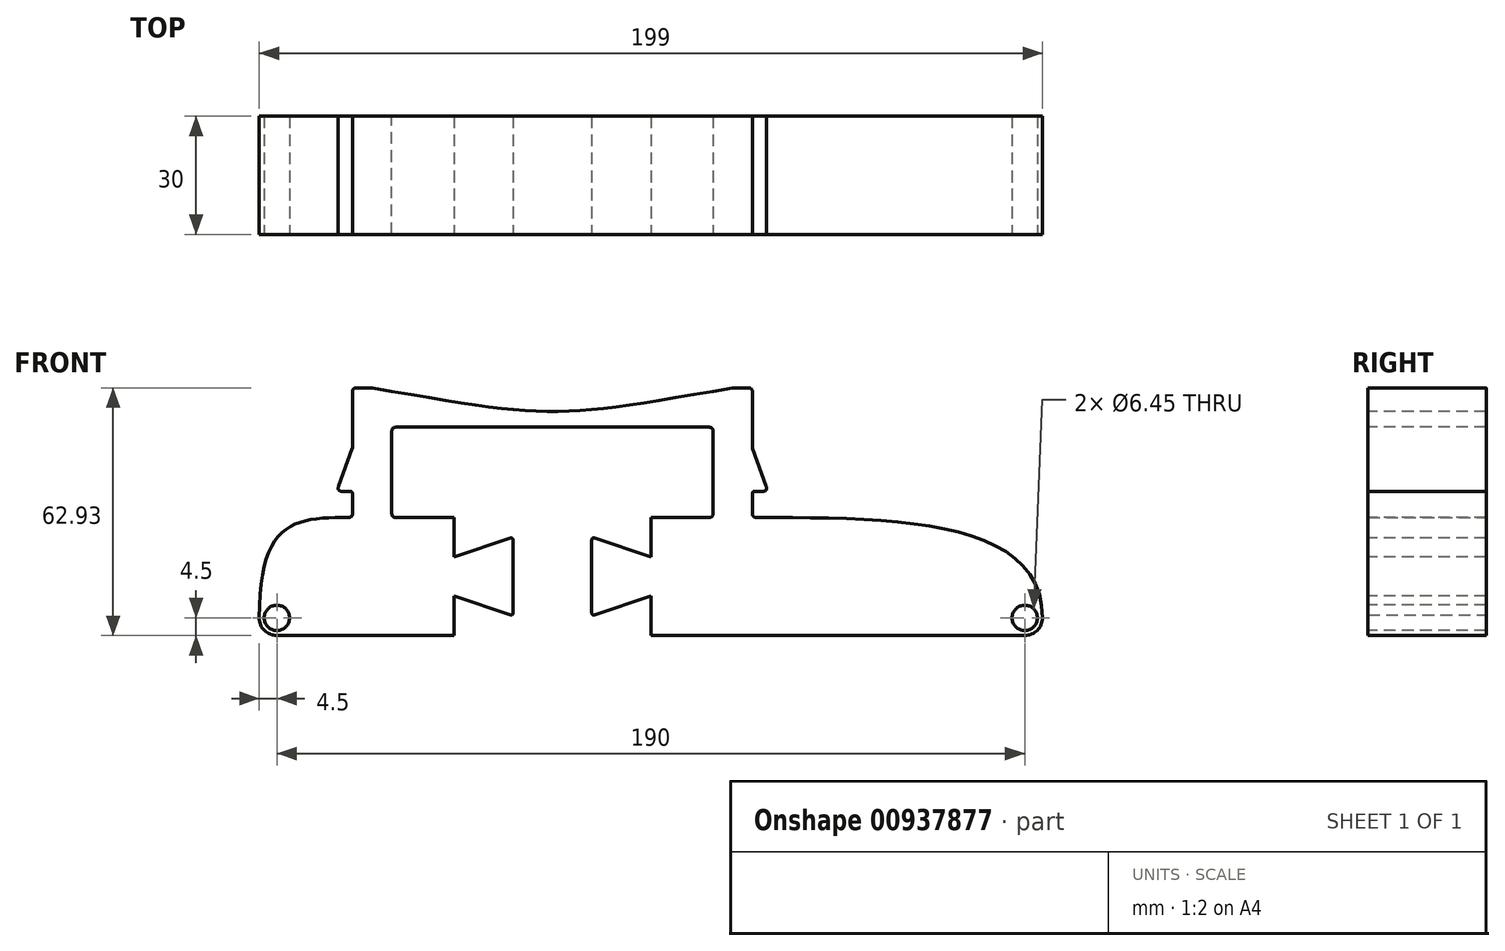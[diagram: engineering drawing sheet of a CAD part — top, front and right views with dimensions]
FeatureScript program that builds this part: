
annotation { "Feature Type Name" : "Feature", "Feature Type Description" : "" }
export const myFeature = defineFeature(function(context is Context, id is Id, definition is map)
    precondition{}
    {
        {
            var Q0;
            Q0=qCreatedBy(makeId("Front.planeOp"),FACE);
            var sketch = newSketch(context, id + "F0", { "sketchPlane" : qUnion([Q0])});
            skLineSegment(sketch, "E0", {"start": v(0, 0) * mm, "end": v(-70, 0) * mm});
            skLineSegment(sketch, "E1", {"start": v(-50.8, 30) * mm, "end": v(-50.8, 36.63) * mm});
            skLineSegment(sketch, "E2", {"start": v(-50.8, 36.63) * mm, "end": v(-52.8, 36.63) * mm});
            skLineSegment(sketch, "E3", {"start": v(-52.8, 36.63) * mm, "end": v(-52.8, 36.63) * mm});
            skLineSegment(sketch, "E4", {"start": v(-52.8, 36.63) * mm, "end": v(-54.8, 36.63) * mm});
            skLineSegment(sketch, "E5", {"start": v(-54.8, 36.63) * mm, "end": v(-54.8, 36.63) * mm});
            skLineSegment(sketch, "E6", {"start": v(-50.8, 47.63) * mm, "end": v(-50.8, 62.93) * mm});
            skPoint(sketch, "E7", {"position": v(-70, 4.5) * mm});
            skCircle(sketch, "E8", {"center": v(-70, 4.5) * mm, "radius": 4.5 * mm});
            skLineSegment(sketch, "E9", {"start": v(-50.8, 30) * mm, "end": v(-73.18, 7.69) * mm});
            skLineSegment(sketch, "E10", {"start": v(50.8, 62.93) * mm, "end": v(50.8, 47.63) * mm});
            skLineSegment(sketch, "E11", {"start": v(54.8, 36.63) * mm, "end": v(52.8, 36.63) * mm});
            skLineSegment(sketch, "E12", {"start": v(52.8, 36.63) * mm, "end": v(52.8, 36.63) * mm});
            skLineSegment(sketch, "E13", {"start": v(52.8, 36.63) * mm, "end": v(50.8, 36.63) * mm});
            skLineSegment(sketch, "E14", {"start": v(50.8, 36.63) * mm, "end": v(50.8, 30) * mm});
            skLineSegment(sketch, "E15", {"start": v(120, 0) * mm, "end": v(0, 0) * mm});
            skCircle(sketch, "E16", {"center": v(120, 4.5) * mm, "radius": 4.5 * mm});
            skLineSegment(sketch, "E17", {"start": v(50.8, 30) * mm, "end": v(121.3, 8.8) * mm});
            skLineSegment(sketch, "E18", {"start": v(-50.8, 62.93) * mm, "end": v(-40.8, 62.93) * mm});
            skPoint(sketch, "E19", {"position": v(0, 62.93) * mm});
            skLineSegment(sketch, "E20", {"start": v(-50.8, 47.63) * mm, "end": v(-54.8, 36.63) * mm});
            skLineSegment(sketch, "E21", {"start": v(50.8, 47.63) * mm, "end": v(54.8, 36.63) * mm});
            skLineSegment(sketch, "E22", {"start": v(54.8, 36.63) * mm, "end": v(54.8, 36.63) * mm});
            skPoint(sketch, "E23.1.internal.snap0", {"position": v(86.05, 19.4) * mm});
            skPoint(sketch, "E24", {"position": v(-61.99, 18.84) * mm});
            skFitSpline(sketch, "E25", {"points": [v(124.5, 4.5) * mm, v(50.8, 30) * mm, v(-50.8, 30) * mm, v(-74.5, 4.5) * mm], "startDerivative": vector(0, 214.93) * mm, "endDerivative": vector(0, -321.69) * mm});
            skLineSegment(sketch, "E26", {"start": v(-40.8, 62.93) * mm, "end": v(-40.8, 30) * mm});
            skLineSegment(sketch, "E27", {"start": v(40.8, 62.93) * mm, "end": v(40.8, 30) * mm});
            skLineSegment(sketch, "E28", {"start": v(-40.8, 62.93) * mm, "end": v(40.8, 62.93) * mm});
            skLineSegment(sketch, "E29", {"start": v(40.8, 62.93) * mm, "end": v(50.8, 62.93) * mm});
            skCircle(sketch, "E30", {"center": v(-70, 4.5) * mm, "radius": 3.18 * mm});
            skLineSegment(sketch, "E31", {"start": v(-10, 30) * mm, "end": v(-10, 20) * mm});
            skLineSegment(sketch, "E32", {"start": v(-10, 20) * mm, "end": v(-10, 10) * mm});
            skLineSegment(sketch, "E33", {"start": v(-10, 10) * mm, "end": v(-10, 0) * mm});
            skLineSegment(sketch, "E34", {"start": v(-25, 30) * mm, "end": v(-25, 20) * mm});
            skLineSegment(sketch, "E35", {"start": v(-25, 20) * mm, "end": v(-25, 10) * mm});
            skLineSegment(sketch, "E36", {"start": v(-25, 10) * mm, "end": v(-25, 0) * mm});
            skLineSegment(sketch, "E37", {"start": v(-25, 10) * mm, "end": v(-10, 5) * mm});
            skLineSegment(sketch, "E38", {"start": v(-25, 20) * mm, "end": v(-10, 25) * mm});
            skLineSegment(sketch, "E39", {"start": v(10, 30) * mm, "end": v(10, 20) * mm});
            skLineSegment(sketch, "E40", {"start": v(10, 20) * mm, "end": v(10, 10) * mm});
            skLineSegment(sketch, "E41", {"start": v(10, 10) * mm, "end": v(10, 0) * mm});
            skLineSegment(sketch, "E42", {"start": v(25, 30) * mm, "end": v(25, 20) * mm});
            skLineSegment(sketch, "E43", {"start": v(25, 20) * mm, "end": v(25, 10) * mm});
            skLineSegment(sketch, "E44", {"start": v(25, 10) * mm, "end": v(25, 0) * mm});
            skLineSegment(sketch, "E45", {"start": v(25, 20) * mm, "end": v(10, 25) * mm});
            skLineSegment(sketch, "E46", {"start": v(25, 10) * mm, "end": v(10, 5) * mm});
            skLineSegment(sketch, "E47", {"start": v(-25, 25) * mm, "end": v(-10, 20) * mm});
            skLineSegment(sketch, "E48", {"start": v(-10, 10) * mm, "end": v(-25, 5) * mm});
            skLineSegment(sketch, "E49", {"start": v(25, 25) * mm, "end": v(10, 20) * mm});
            skLineSegment(sketch, "E50", {"start": v(10, 10) * mm, "end": v(25, 5) * mm});
            skLineSegment(sketch, "E51", {"start": v(-40.8, 52.93) * mm, "end": v(40.8, 52.93) * mm});
            skFitSpline(sketch, "E52", {"points": [v(-45.8, 62.93) * mm, v(45.8, 62.93) * mm], "startDerivative": vector(137.4, -24) * mm, "endDerivative": vector(137.4, 24) * mm});
            skSolve(sketch);
        }
        {
            var Q0;
            Q0=makeQuery(id+"F0.imprint","IMPRINT",FACE,{"disambiguationData":[TD([[makeQuery(id+"F0.imprint","IMPRINT",EDGE,{"derivedFrom":sQuery(id+"F0.wireOp",EDGE,"E1")}),-1.0]])]});
            var Q1;
            {var subQ0=sQuery(id+"F0.wireOp",EDGE,"E8");var subQ1=makeQuery(id+"F0.imprint","INTERSECT",VERTEX,{"derivedFrom":[subQ0,sQuery(id+"F0.wireOp",EDGE,"E9")]});Q1=makeQuery(id+"F0.imprint","IMPRINT",FACE,{"disambiguationData":[TD([[makeQuery(id+"F0.imprint","IMPRINT",EDGE,{"disambiguationData":[TD([[subQ1,-1.0]])],"derivedFrom":subQ0}),1.0]])]});}
            var Q2;
            Q2=makeQuery(id+"F0.imprint","IMPRINT",FACE,{"disambiguationData":[TD([[makeQuery(id+"F0.imprint","IMPRINT",EDGE,{"derivedFrom":sQuery(id+"F0.wireOp",EDGE,"7cihORvh-BMdg-jHTC-DTSp-j1uDXrcYjoYH")}),1.0]])]});
            var Q3;
            {var subQ0=sQuery(id+"F0.wireOp",EDGE,"E16");var subQ1=makeQuery(id+"F0.imprint","INTERSECT",VERTEX,{"derivedFrom":[sQuery(id+"F0.wireOp",EDGE,"E15"),subQ0]});Q3=makeQuery(id+"F0.imprint","IMPRINT",FACE,{"disambiguationData":[TD([[makeQuery(id+"F0.imprint","IMPRINT",EDGE,{"disambiguationData":[TD([[subQ1,1.0]])],"derivedFrom":subQ0}),1.0]])]});}
            var Q4;
            Q4=makeQuery(id+"F0.imprint","IMPRINT",FACE,{"disambiguationData":[TD([[makeQuery(id+"F0.imprint","IMPRINT",EDGE,{"derivedFrom":sQuery(id+"F0.wireOp",EDGE,"4cD9h1So-SKgd-zRkL-ZQbT-vk3D5KubyaQk")}),1.0]])]});
            var Q5;
            {var subQ0=sQuery(id+"F0.wireOp",EDGE,"E17");Q5=makeQuery(id+"F0.imprint","IMPRINT",FACE,{"disambiguationData":[TD([[makeQuery(id+"F0.imprint","IMPRINT",EDGE,{"derivedFrom":subQ0}),1.0]])]});}
            var Q6;
            {var subQ0=sQuery(id+"F0.wireOp",EDGE,"E9");Q6=makeQuery(id+"F0.imprint","IMPRINT",FACE,{"disambiguationData":[TD([[makeQuery(id+"F0.imprint","IMPRINT",EDGE,{"derivedFrom":subQ0}),-1.0]])]});}
            var Q7;
            Q7=makeQuery(id+"F0.imprint","IMPRINT",FACE,{"disambiguationData":[TD([[makeQuery(id+"F0.imprint","IMPRINT",EDGE,{"derivedFrom":sQuery(id+"F0.wireOp",EDGE,"E10")}),-1.0]])]});
            var Q8;
            Q8=makeQuery(id+"F0.imprint","IMPRINT",FACE,{"disambiguationData":[TD([[makeQuery(id+"F0.imprint","IMPRINT",EDGE,{"derivedFrom":sQuery(id+"F0.wireOp",EDGE,"E11")}),-1.0]])]});
            var Q9;
            {var subQ0=sQuery(id+"F0.wireOp",EDGE,"E9");Q9=makeQuery(id+"F0.imprint","IMPRINT",FACE,{"disambiguationData":[TD([[makeQuery(id+"F0.imprint","IMPRINT",EDGE,{"derivedFrom":subQ0}),1.0]])]});}
            var Q10;
            {var subQ1=sQuery(id+"F0.wireOp",EDGE,"E17");Q10=makeQuery(id+"F0.imprint","IMPRINT",FACE,{"disambiguationData":[TD([[makeQuery(id+"F0.imprint","IMPRINT",EDGE,{"derivedFrom":subQ1}),-1.0]])]});}
            var Q11;
            {var subQ1=sQuery(id+"F0.wireOp",EDGE,"E31");var subQ3=sQuery(id+"F0.wireOp",EDGE,"E38");var subQ4=makeQuery(id+"F0.imprint","INTERSECT",VERTEX,{"derivedFrom":[subQ1,subQ3]});Q11=makeQuery(id+"F0.imprint","IMPRINT",FACE,{"disambiguationData":[TD([[makeQuery(id+"F0.imprint","IMPRINT",EDGE,{"disambiguationData":[TD([[subQ4,1.0]])],"derivedFrom":subQ3}),-1.0]])]});}
            var Q12;
            {var subQ1=sQuery(id+"F0.wireOp",EDGE,"E39");var subQ3=sQuery(id+"F0.wireOp",EDGE,"E45");var subQ4=makeQuery(id+"F0.imprint","INTERSECT",VERTEX,{"derivedFrom":[subQ1,subQ3]});Q12=makeQuery(id+"F0.imprint","IMPRINT",FACE,{"disambiguationData":[TD([[makeQuery(id+"F0.imprint","IMPRINT",EDGE,{"disambiguationData":[TD([[subQ4,1.0]])],"derivedFrom":subQ3}),1.0]])]});}
            var Q13;
            {var subQ7=sQuery(id+"F0.wireOp",EDGE,"E32");Q13=makeQuery(id+"F0.imprint","IMPRINT",FACE,{"disambiguationData":[TD([[makeQuery(id+"F0.imprint","IMPRINT",EDGE,{"derivedFrom":subQ7}),-1.0]])]});}
            var Q14;
            {var subQ1=sQuery(id+"F0.wireOp",EDGE,"E33");var subQ3=sQuery(id+"F0.wireOp",EDGE,"E37");var subQ4=makeQuery(id+"F0.imprint","INTERSECT",VERTEX,{"derivedFrom":[subQ1,subQ3]});Q14=makeQuery(id+"F0.imprint","IMPRINT",FACE,{"disambiguationData":[TD([[makeQuery(id+"F0.imprint","IMPRINT",EDGE,{"disambiguationData":[TD([[subQ4,1.0]])],"derivedFrom":subQ3}),1.0]])]});}
            var Q15;
            {var subQ7=sQuery(id+"F0.wireOp",EDGE,"E40");Q15=makeQuery(id+"F0.imprint","IMPRINT",FACE,{"disambiguationData":[TD([[makeQuery(id+"F0.imprint","IMPRINT",EDGE,{"derivedFrom":subQ7}),1.0]])]});}
            var Q16;
            {var subQ1=sQuery(id+"F0.wireOp",EDGE,"E41");var subQ3=sQuery(id+"F0.wireOp",EDGE,"E46");var subQ4=makeQuery(id+"F0.imprint","INTERSECT",VERTEX,{"derivedFrom":[subQ1,subQ3]});Q16=makeQuery(id+"F0.imprint","IMPRINT",FACE,{"disambiguationData":[TD([[makeQuery(id+"F0.imprint","IMPRINT",EDGE,{"disambiguationData":[TD([[subQ4,1.0]])],"derivedFrom":subQ3}),-1.0]])]});}
            var Q17;
            {var subQ0=sQuery(id+"F0.wireOp",EDGE,"E51");Q17=makeQuery(id+"F0.imprint","IMPRINT",FACE,{"disambiguationData":[TD([[makeQuery(id+"F0.imprint","IMPRINT",EDGE,{"derivedFrom":subQ0}),1.0]])]});}
            extrude(context, id + "F1", {"entities" : qUnion([Q0, Q1, Q2, Q3, Q4, Q5, Q6, Q7, Q8, Q9, Q10, Q11, Q12, Q13, Q14, Q15, Q16, Q17]), "oppositeDirection" : true, "depth" : 30 * mm, "offsetDistance" : 25 * mm});
        }
        {
            var Q0;
            Q0=sQuery(id+"F0.wireOp",VERTEX,"E7");
            var Q1;
            Q1=sQuery(id+"F0.wireOp",VERTEX,"E16.center");
            var Q2;
            Q2=makeQuery(id+"F1.opExtrude","SWEPT_BODY",BODY,{"disambiguationData":[OSD([sQuery(id+"F0.wireOp",EDGE,"E0"),sQuery(id+"F0.wireOp",EDGE,"pubzkyvZ-cRVs-HS7m-mzxW-3LitaN00uNvF"),sQuery(id+"F0.wireOp",EDGE,"w8PnYHh2-jLbr-hi3E-DdNM-35XMNPo8wsM1"),sQuery(id+"F0.wireOp",EDGE,"E1"),sQuery(id+"F0.wireOp",EDGE,"E2"),sQuery(id+"F0.wireOp",EDGE,"E3"),sQuery(id+"F0.wireOp",EDGE,"E4"),sQuery(id+"F0.wireOp",EDGE,"E5"),sQuery(id+"F0.wireOp",EDGE,"QAPtyPks-H0dY-mEL7-AEC2-er1j7m6l4yYA"),sQuery(id+"F0.wireOp",EDGE,"E6"),sQuery(id+"F0.wireOp",EDGE,"AgmpphwO-VWOp-YMGR-kliC-7jdcb5ISksbA"),sQuery(id+"F0.wireOp",EDGE,"4cD9h1So-SKgd-zRkL-ZQbT-vk3D5KubyaQk"),sQuery(id+"F0.wireOp",EDGE,"uP0SVVGF-vnew-W4Ng-l7U9-sh23WeTH0zID"),sQuery(id+"F0.wireOp",EDGE,"7cihORvh-BMdg-jHTC-DTSp-j1uDXrcYjoYH")])]});
            hole(context, id + "F2", {"style" : HoleStyle.SIMPLE, "endStyle" : HoleEndStyle.THROUGH, "holeDiameter" : 6.35 * mm + .1 * mm, "majorDiameter" : 5 * mm, "isTappedThrough" : true, "tappedDepth" : 12 * mm, "tapClearance" : 3, "locations" : qUnion([Q0, Q1]), "scope" : qUnion([Q2])});
        }
        {
            var Q0;
            Q0=makeQuery(id+"F1.opExtrude","SWEPT_EDGE",EDGE,{"disambiguationData":[OSD([sQuery(id+"F0.wireOp",EDGE,"w8PnYHh2-jLbr-hi3E-DdNM-35XMNPo8wsM1"),sQuery(id+"F0.wireOp",EDGE,"E1"),sQuery(id+"F0.wireOp",EDGE,"E9")])]});
            var Q1;
            Q1=makeQuery(id+"F1.opExtrude","SWEPT_EDGE",EDGE,{"disambiguationData":[OSD([sQuery(id+"F0.wireOp",EDGE,"E14"),sQuery(id+"F0.wireOp",EDGE,"E17")])]});
            var Q2;
            Q2=makeQuery(id+"F1.opExtrude","SWEPT_EDGE",EDGE,{"disambiguationData":[OSD([sQuery(id+"F0.wireOp",EDGE,"E21"),sQuery(id+"F0.wireOp",EDGE,"E29")])]});
            var Q3;
            Q3=makeQuery(id+"F1.opExtrude","SWEPT_EDGE",EDGE,{"disambiguationData":[OSD([sQuery(id+"F0.wireOp",EDGE,"E27"),sQuery(id+"F0.wireOp",EDGE,"E28"),sQuery(id+"F0.wireOp",EDGE,"E29")])]});
            var Q4;
            Q4=makeQuery(id+"F1.opExtrude","SWEPT_EDGE",EDGE,{"disambiguationData":[OSD([sQuery(id+"F0.wireOp",EDGE,"E18"),sQuery(id+"F0.wireOp",EDGE,"E26"),sQuery(id+"F0.wireOp",EDGE,"E28")])]});
            var Q5;
            Q5=makeQuery(id+"F1.opExtrude","SWEPT_EDGE",EDGE,{"disambiguationData":[OSD([sQuery(id+"F0.wireOp",EDGE,"E18"),sQuery(id+"F0.wireOp",EDGE,"E20")])]});
            fillet(context, id + "F3", {"entities" : qUnion([Q0, Q1, Q2, Q3, Q4, Q5]), "radius" : 1 * mm, "tangentPropagation" : true, "rho" : .5, "crossSection" : FilletCrossSection.CONIC, "allowEdgeOverflow" : false});
        }
        {
            var Q0;
            Q0=makeQuery(id+"F1.opExtrude","SWEPT_EDGE",EDGE,{"disambiguationData":[OSD([sQuery(id+"F0.wireOp",EDGE,"E1"),sQuery(id+"F0.wireOp",EDGE,"E2")])]});
            var Q1;
            Q1=makeQuery(id+"F1.opExtrude","SWEPT_EDGE",EDGE,{"disambiguationData":[OSD([sQuery(id+"F0.wireOp",EDGE,"E6"),sQuery(id+"F0.wireOp",EDGE,"E20")])]});
            var Q2;
            Q2=makeQuery(id+"F1.opExtrude","SWEPT_EDGE",EDGE,{"disambiguationData":[OSD([sQuery(id+"F0.wireOp",EDGE,"E5"),sQuery(id+"F0.wireOp",EDGE,"E20")])]});
            var Q3;
            Q3=makeQuery(id+"F1.opExtrude","SWEPT_EDGE",EDGE,{"disambiguationData":[OSD([sQuery(id+"F0.wireOp",EDGE,"E13"),sQuery(id+"F0.wireOp",EDGE,"E14")])]});
            var Q4;
            Q4=makeQuery(id+"F1.opExtrude","SWEPT_EDGE",EDGE,{"disambiguationData":[OSD([sQuery(id+"F0.wireOp",EDGE,"E12"),sQuery(id+"F0.wireOp",EDGE,"E13")])]});
            var Q5;
            Q5=makeQuery(id+"F1.opExtrude","SWEPT_EDGE",EDGE,{"disambiguationData":[OSD([sQuery(id+"F0.wireOp",EDGE,"E11"),sQuery(id+"F0.wireOp",EDGE,"E12")])]});
            var Q6;
            Q6=makeQuery(id+"F1.opExtrude","SWEPT_EDGE",EDGE,{"disambiguationData":[OSD([sQuery(id+"F0.wireOp",EDGE,"E11"),sQuery(id+"F0.wireOp",EDGE,"E22")])]});
            var Q7;
            Q7=makeQuery(id+"F1.opExtrude","SWEPT_EDGE",EDGE,{"disambiguationData":[OSD([sQuery(id+"F0.wireOp",EDGE,"E21"),sQuery(id+"F0.wireOp",EDGE,"E22")])]});
            var Q8;
            Q8=makeQuery(id+"F1.opExtrude","SWEPT_EDGE",EDGE,{"disambiguationData":[OSD([sQuery(id+"F0.wireOp",EDGE,"E10"),sQuery(id+"F0.wireOp",EDGE,"E21")])]});
            var Q9;
            Q9=makeQuery(id+"F1.opExtrude","SWEPT_EDGE",EDGE,{"disambiguationData":[OSD([sQuery(id+"F0.wireOp",EDGE,"E2"),sQuery(id+"F0.wireOp",EDGE,"E3")])]});
            var Q10;
            Q10=makeQuery(id+"F1.opExtrude","SWEPT_EDGE",EDGE,{"disambiguationData":[OSD([sQuery(id+"F0.wireOp",EDGE,"E4"),sQuery(id+"F0.wireOp",EDGE,"E5")])]});
            var Q11;
            Q11=makeQuery(id+"F1.opExtrude","SWEPT_EDGE",EDGE,{"disambiguationData":[OSD([sQuery(id+"F0.wireOp",EDGE,"E3"),sQuery(id+"F0.wireOp",EDGE,"E4")])]});
            var Q12;
            Q12=makeQuery(id+"F1.opExtrude","SWEPT_EDGE",EDGE,{"disambiguationData":[OSD([sQuery(id+"F0.wireOp",EDGE,"E16"),sQuery(id+"F0.wireOp",EDGE,"E25")])]});
            var Q13;
            Q13=makeQuery(id+"F1.opExtrude","SWEPT_EDGE",EDGE,{"disambiguationData":[OSD([sQuery(id+"F0.wireOp",EDGE,"E8"),sQuery(id+"F0.wireOp",EDGE,"E25")])]});
            fillet(context, id + "F4", {"entities" : qUnion([Q0, Q1, Q2, Q3, Q4, Q5, Q6, Q7, Q8, Q9, Q10, Q11, Q12, Q13]), "radius" : .5 * mm, "tangentPropagation" : true, "allowEdgeOverflow" : false});
        }
        {
            var Q0;
            Q0=makeQuery(id+"F1.opExtrude","SWEPT_EDGE",EDGE,{"disambiguationData":[OSD([sQuery(id+"F0.wireOp",EDGE,"E31"),sQuery(id+"F0.wireOp",EDGE,"E38")])]});
            var Q1;
            Q1=makeQuery(id+"F1.opExtrude","SWEPT_EDGE",EDGE,{"disambiguationData":[OSD([sQuery(id+"F0.wireOp",EDGE,"E33"),sQuery(id+"F0.wireOp",EDGE,"E37")])]});
            var Q2;
            Q2=makeQuery(id+"F1.opExtrude","SWEPT_EDGE",EDGE,{"disambiguationData":[OSD([sQuery(id+"F0.wireOp",EDGE,"E41"),sQuery(id+"F0.wireOp",EDGE,"E46")])]});
            var Q3;
            Q3=makeQuery(id+"F1.opExtrude","SWEPT_EDGE",EDGE,{"disambiguationData":[OSD([sQuery(id+"F0.wireOp",EDGE,"E39"),sQuery(id+"F0.wireOp",EDGE,"E45")])]});
            fillet(context, id + "F5", {"entities" : qUnion([Q0, Q1, Q2, Q3]), "radius" : .5 * mm, "tangentPropagation" : true, "allowEdgeOverflow" : false});
        }
    });
